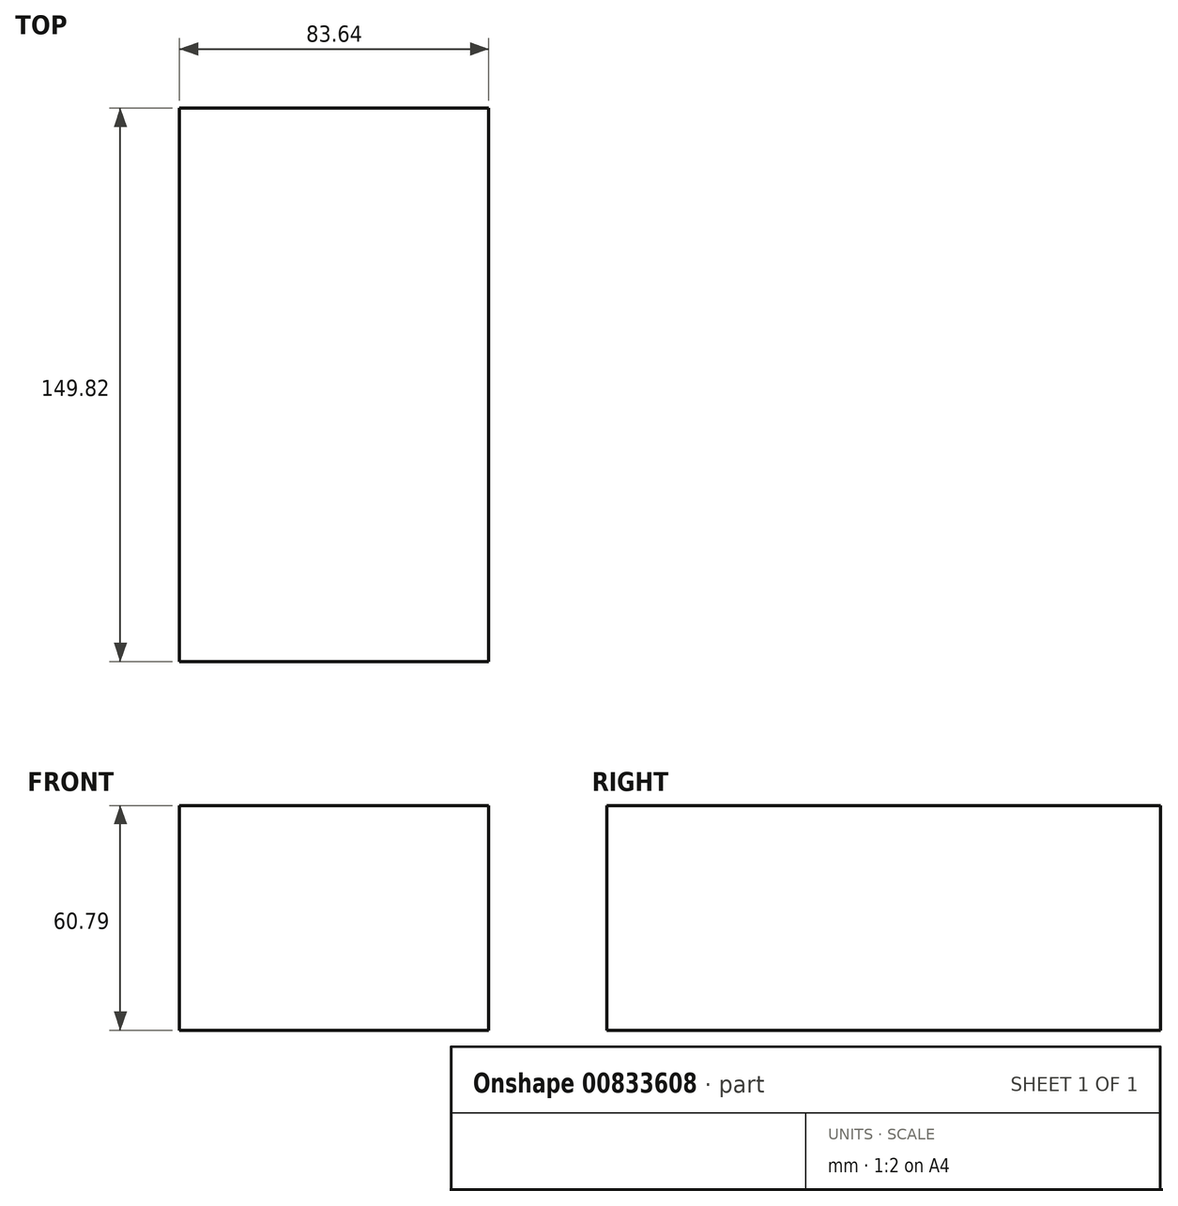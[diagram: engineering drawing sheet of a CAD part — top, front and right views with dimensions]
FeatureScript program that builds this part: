
annotation { "Feature Type Name" : "Feature", "Feature Type Description" : "" }
export const myFeature = defineFeature(function(context is Context, id is Id, definition is map)
    precondition{}
    {
        {
            var Q0;
            Q0=qCreatedBy(makeId("Front.planeOp"),FACE);
            var sketch = newSketch(context, id + "F0", { "sketchPlane" : qUnion([Q0])});
            skLineSegment(sketch, "E0.bottom", {"start": v(31.78, 32.15) * mm, "end": v(-51.86, 32.15) * mm});
            skLineSegment(sketch, "E0.top", {"start": v(31.78, -28.64) * mm, "end": v(-51.86, -28.64) * mm});
            skLineSegment(sketch, "E0.left", {"start": v(31.78, 32.15) * mm, "end": v(31.78, -28.64) * mm});
            skLineSegment(sketch, "E0.right", {"start": v(-51.86, 32.15) * mm, "end": v(-51.86, -28.64) * mm});
            skSolve(sketch);
        }
        {
            var Q0;
            Q0=makeQuery(id+"F0.imprint","IMPRINT",FACE,{"disambiguationData":[TD([[makeQuery(id+"F0.imprint","IMPRINT",EDGE,{"derivedFrom":sQuery(id+"F0.wireOp",EDGE,"E0.bottom")}),1.0]])]});
            extrude(context, id + "F1", {"entities" : qUnion([Q0]), "depth" : 149.82 * mm, "offsetDistance" : 25.4 * mm});
        }
    });
